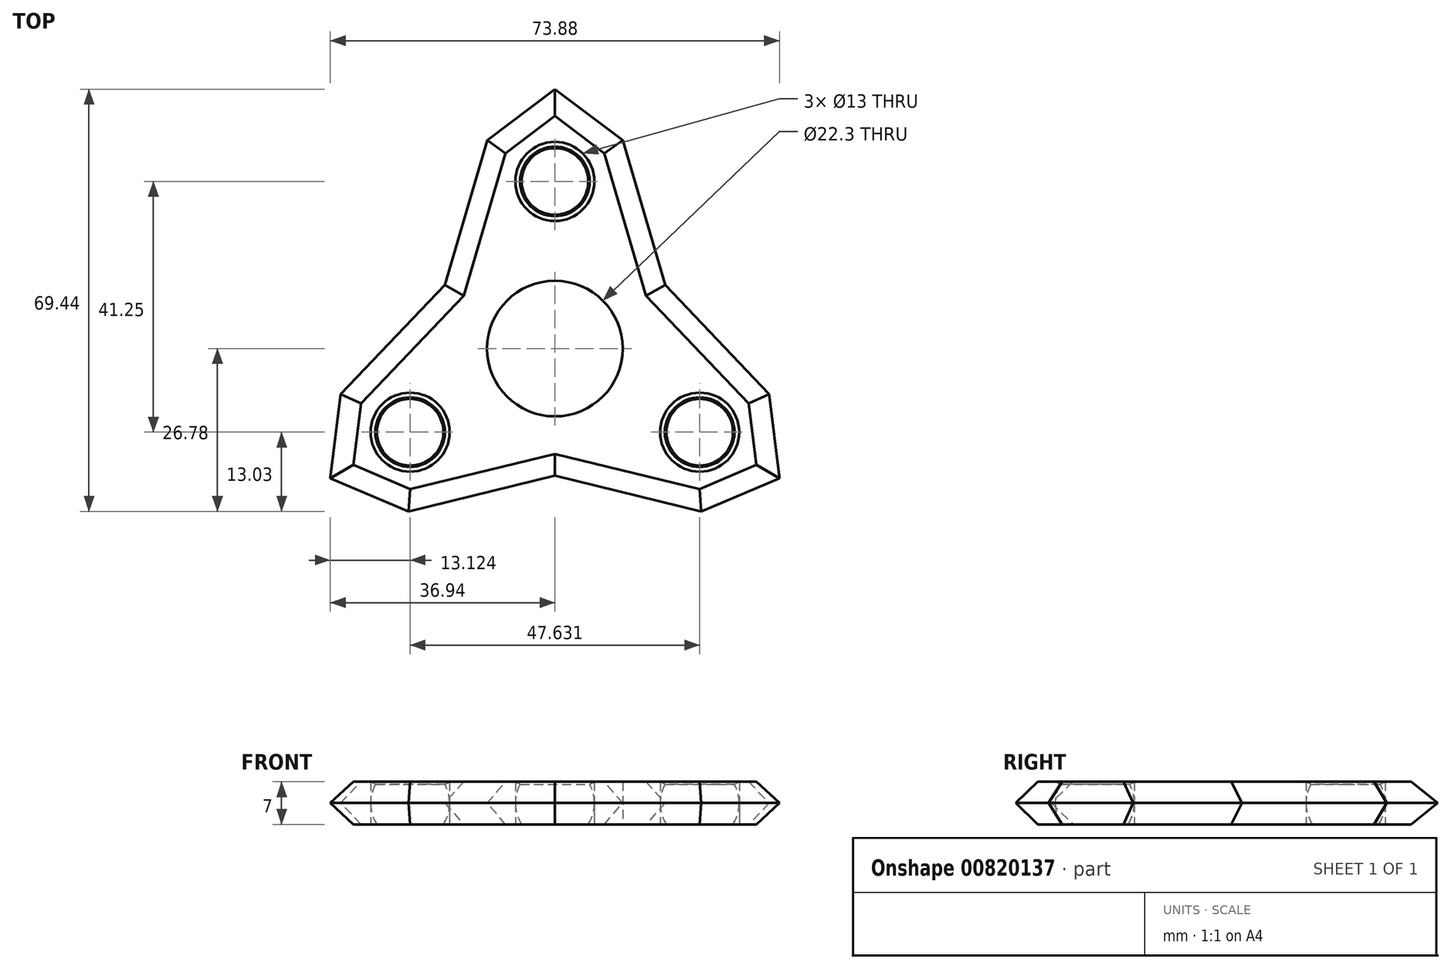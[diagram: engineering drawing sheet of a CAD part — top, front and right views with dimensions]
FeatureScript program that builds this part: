
annotation { "Feature Type Name" : "Feature", "Feature Type Description" : "" }
export const myFeature = defineFeature(function(context is Context, id is Id, definition is map)
    precondition{}
    {
        {
            var Q0;
            Q0=qCreatedBy(makeId("Top.planeOp"),FACE);
            var sketch = newSketch(context, id + "F0", { "sketchPlane" : qUnion([Q0])});
            skCircle(sketch, "E0", {"center": v(0, 0) * mm, "radius": 11.15 * mm});
            skCircle(sketch, "E1", {"center": v(0, 27.5) * mm, "radius": 6.5 * mm});
            skLineSegment(sketch, "E2", {"start": v(0, 27.5) * mm, "end": v(0, 0) * mm});
            skCircle(sketch, "E3", {"center": v(0, 0) * mm, "radius": 14.15 * mm});
            skCircle(sketch, "E4", {"center": v(0, 27.5) * mm, "radius": 9.5 * mm});
            skLineSegment(sketch, "E5", {"start": v(0, 42.66) * mm, "end": v(11.14, 34.25) * mm});
            skLineSegment(sketch, "E6", {"start": v(0, 0) * mm, "end": v(12.25, 7.08) * mm});
            skLineSegment(sketch, "E7", {"start": v(12.25, 7.08) * mm, "end": v(39.54, 22.83) * mm});
            skLineSegment(sketch, "E8", {"start": v(11.14, 34.25) * mm, "end": v(18.13, 10.46) * mm});
            skLineSegment(sketch, "E9.MirrorCS", {"start": v(35.23, -7.47) * mm, "end": v(18.13, 10.46) * mm});
            skLineSegment(sketch, "E10.MirrorCS", {"start": v(36.94, -21.33) * mm, "end": v(35.23, -7.47) * mm});
            skLineSegment(sketch, "E11.MirrorCS", {"start": v(0, 42.66) * mm, "end": v(-11.14, 34.25) * mm});
            skLineSegment(sketch, "E12.MirrorCS", {"start": v(-11.14, 34.25) * mm, "end": v(-18.13, 10.46) * mm});
            skLineSegment(sketch, "E13.MirrorCS", {"start": v(-35.23, -7.47) * mm, "end": v(-18.13, 10.46) * mm});
            skLineSegment(sketch, "E14.MirrorCS", {"start": v(-36.94, -21.33) * mm, "end": v(-35.23, -7.47) * mm});
            skLineSegment(sketch, "E15.MirrorCS", {"start": v(-24.09, -26.78) * mm, "end": v(0, -20.93) * mm});
            skLineSegment(sketch, "E16.MirrorCS", {"start": v(-36.94, -21.33) * mm, "end": v(-24.09, -26.78) * mm});
            skLineSegment(sketch, "E17.MirrorCS", {"start": v(24.09, -26.78) * mm, "end": v(0, -20.93) * mm});
            skLineSegment(sketch, "E18.MirrorCS", {"start": v(36.94, -21.33) * mm, "end": v(24.09, -26.78) * mm});
            skCircle(sketch, "E19.1.0", {"center": v(-23.82, -13.75) * mm, "radius": 9.5 * mm});
            skCircle(sketch, "E19.1.1", {"center": v(-23.82, -13.75) * mm, "radius": 6.5 * mm});
            skCircle(sketch, "E19.2.0", {"center": v(23.82, -13.75) * mm, "radius": 9.5 * mm});
            skCircle(sketch, "E19.2.1", {"center": v(23.82, -13.75) * mm, "radius": 6.5 * mm});
            skSolve(sketch);
        }
        {
            var Q0;
            {var subQ0=sQuery(id+"F0.wireOp",EDGE,"E2");var subQ1=sQuery(id+"F0.wireOp",EDGE,"E0");var subQ2=makeQuery(id+"F0.imprint","INTERSECT",VERTEX,{"derivedFrom":[subQ1,subQ0]});Q0=makeQuery(id+"F0.imprint","IMPRINT",FACE,{"disambiguationData":[TD([[makeQuery(id+"F0.imprint","IMPRINT",EDGE,{"disambiguationData":[TD([[subQ2,-1.0]])],"derivedFrom":subQ1}),-1.0]])]});}
            var Q1;
            Q1=makeQuery(id+"F0.imprint","IMPRINT",FACE,{"disambiguationData":[TD([[makeQuery(id+"F0.imprint","IMPRINT",EDGE,{"derivedFrom":sQuery(id+"F0.wireOp",EDGE,"E4")}),-1.0]])]});
            var Q2;
            {var subQ0=sQuery(id+"F0.wireOp",EDGE,"E2");var subQ1=sQuery(id+"F0.wireOp",EDGE,"E0");var subQ2=makeQuery(id+"F0.imprint","INTERSECT",VERTEX,{"derivedFrom":[subQ1,subQ0]});Q2=makeQuery(id+"F0.imprint","IMPRINT",FACE,{"disambiguationData":[TD([[makeQuery(id+"F0.imprint","IMPRINT",EDGE,{"disambiguationData":[TD([[subQ2,1.0]])],"derivedFrom":subQ1}),-1.0]])]});}
            var Q3;
            Q3=makeQuery(id+"F0.imprint","IMPRINT",FACE,{"disambiguationData":[TD([[makeQuery(id+"F0.imprint","IMPRINT",EDGE,{"derivedFrom":sQuery(id+"F0.wireOp",EDGE,"E19.2.0")}),1.0]])]});
            var Q4;
            Q4=makeQuery(id+"F0.imprint","IMPRINT",FACE,{"disambiguationData":[TD([[makeQuery(id+"F0.imprint","IMPRINT",EDGE,{"derivedFrom":sQuery(id+"F0.wireOp",EDGE,"E1")}),-1.0]])]});
            var Q5;
            Q5=makeQuery(id+"F0.imprint","IMPRINT",FACE,{"disambiguationData":[TD([[makeQuery(id+"F0.imprint","IMPRINT",EDGE,{"derivedFrom":sQuery(id+"F0.wireOp",EDGE,"E19.1.0")}),1.0]])]});
            extrude(context, id + "F1", {"entities" : qUnion([Q0, Q1, Q2, Q3, Q4, Q5]), "depth" : 7 * mm, "offsetDistance" : 25 * mm});
        }
        {
            var Q0;
            Q0=makeQuery(id+"F1.opExtrude","CAP_EDGE",EDGE,{"disambiguationData":[OSD([sQuery(id+"F0.wireOp",EDGE,"E15.MirrorCS")])],"isStart":true});
            var Q1;
            Q1=makeQuery(id+"F1.opExtrude","CAP_EDGE",EDGE,{"disambiguationData":[OSD([sQuery(id+"F0.wireOp",EDGE,"E16.MirrorCS")])],"isStart":true});
            var Q2;
            Q2=makeQuery(id+"F1.opExtrude","CAP_EDGE",EDGE,{"disambiguationData":[OSD([sQuery(id+"F0.wireOp",EDGE,"E14.MirrorCS")])],"isStart":true});
            var Q3;
            Q3=makeQuery(id+"F1.opExtrude","CAP_EDGE",EDGE,{"disambiguationData":[OSD([sQuery(id+"F0.wireOp",EDGE,"E13.MirrorCS")])],"isStart":true});
            var Q4;
            Q4=makeQuery(id+"F1.opExtrude","CAP_EDGE",EDGE,{"disambiguationData":[OSD([sQuery(id+"F0.wireOp",EDGE,"E12.MirrorCS")])],"isStart":true});
            var Q5;
            Q5=makeQuery(id+"F1.opExtrude","CAP_EDGE",EDGE,{"disambiguationData":[OSD([sQuery(id+"F0.wireOp",EDGE,"E11.MirrorCS")])],"isStart":true});
            var Q6;
            Q6=makeQuery(id+"F1.opExtrude","CAP_EDGE",EDGE,{"disambiguationData":[OSD([sQuery(id+"F0.wireOp",EDGE,"E5")])],"isStart":true});
            var Q7;
            Q7=makeQuery(id+"F1.opExtrude","CAP_EDGE",EDGE,{"disambiguationData":[OSD([sQuery(id+"F0.wireOp",EDGE,"E8")])],"isStart":true});
            var Q8;
            Q8=makeQuery(id+"F1.opExtrude","CAP_EDGE",EDGE,{"disambiguationData":[OSD([sQuery(id+"F0.wireOp",EDGE,"E9.MirrorCS")])],"isStart":true});
            var Q9;
            Q9=makeQuery(id+"F1.opExtrude","CAP_EDGE",EDGE,{"disambiguationData":[OSD([sQuery(id+"F0.wireOp",EDGE,"E10.MirrorCS")])],"isStart":true});
            var Q10;
            Q10=makeQuery(id+"F1.opExtrude","CAP_EDGE",EDGE,{"disambiguationData":[OSD([sQuery(id+"F0.wireOp",EDGE,"E18.MirrorCS")])],"isStart":true});
            var Q11;
            Q11=makeQuery(id+"F1.opExtrude","CAP_EDGE",EDGE,{"disambiguationData":[OSD([sQuery(id+"F0.wireOp",EDGE,"E17.MirrorCS")])],"isStart":true});
            var Q12;
            Q12=makeQuery(id+"F1.opExtrude","CAP_EDGE",EDGE,{"disambiguationData":[OSD([sQuery(id+"F0.wireOp",EDGE,"E5")])],"isStart":false});
            var Q13;
            Q13=makeQuery(id+"F1.opExtrude","CAP_EDGE",EDGE,{"disambiguationData":[OSD([sQuery(id+"F0.wireOp",EDGE,"E11.MirrorCS")])],"isStart":false});
            var Q14;
            Q14=makeQuery(id+"F1.opExtrude","CAP_EDGE",EDGE,{"disambiguationData":[OSD([sQuery(id+"F0.wireOp",EDGE,"E8")])],"isStart":false});
            var Q15;
            Q15=makeQuery(id+"F1.opExtrude","CAP_EDGE",EDGE,{"disambiguationData":[OSD([sQuery(id+"F0.wireOp",EDGE,"E9.MirrorCS")])],"isStart":false});
            var Q16;
            Q16=makeQuery(id+"F1.opExtrude","CAP_EDGE",EDGE,{"disambiguationData":[OSD([sQuery(id+"F0.wireOp",EDGE,"E10.MirrorCS")])],"isStart":false});
            var Q17;
            Q17=makeQuery(id+"F1.opExtrude","CAP_EDGE",EDGE,{"disambiguationData":[OSD([sQuery(id+"F0.wireOp",EDGE,"E18.MirrorCS")])],"isStart":false});
            var Q18;
            Q18=makeQuery(id+"F1.opExtrude","CAP_EDGE",EDGE,{"disambiguationData":[OSD([sQuery(id+"F0.wireOp",EDGE,"E17.MirrorCS")])],"isStart":false});
            var Q19;
            Q19=makeQuery(id+"F1.opExtrude","CAP_EDGE",EDGE,{"disambiguationData":[OSD([sQuery(id+"F0.wireOp",EDGE,"E15.MirrorCS")])],"isStart":false});
            var Q20;
            Q20=makeQuery(id+"F1.opExtrude","CAP_EDGE",EDGE,{"disambiguationData":[OSD([sQuery(id+"F0.wireOp",EDGE,"E16.MirrorCS")])],"isStart":false});
            var Q21;
            Q21=makeQuery(id+"F1.opExtrude","CAP_EDGE",EDGE,{"disambiguationData":[OSD([sQuery(id+"F0.wireOp",EDGE,"E14.MirrorCS")])],"isStart":false});
            var Q22;
            Q22=makeQuery(id+"F1.opExtrude","CAP_EDGE",EDGE,{"disambiguationData":[OSD([sQuery(id+"F0.wireOp",EDGE,"E13.MirrorCS")])],"isStart":false});
            var Q23;
            Q23=makeQuery(id+"F1.opExtrude","CAP_EDGE",EDGE,{"disambiguationData":[OSD([sQuery(id+"F0.wireOp",EDGE,"E12.MirrorCS")])],"isStart":false});
            chamfer(context, id + "F2", {"entities" : qUnion([Q0, Q1, Q2, Q3, Q4, Q5, Q6, Q7, Q8, Q9, Q10, Q11, Q12, Q13, Q14, Q15, Q16, Q17, Q18, Q19, Q20, Q21, Q22, Q23]), "width" : 3.5 * mm, "tangentPropagation" : true});
        }
        {
            var Q0;
            Q0=qCreatedBy(makeId("Right.planeOp"),FACE);
            var sketch = newSketch(context, id + "F3", { "sketchPlane" : qUnion([Q0])});
            skLineSegment(sketch, "E20.0", {"start": v(21, 7) * mm, "end": v(34, 7) * mm});
            skLineSegment(sketch, "E21", {"start": v(21, 0) * mm, "end": v(21, 7) * mm});
            skLineSegment(sketch, "E22", {"start": v(34, 7) * mm, "end": v(34, 0) * mm});
            skLineSegment(sketch, "E23.0", {"start": v(32.15, 0) * mm, "end": v(8.66, 0) * mm});
            skLineSegment(sketch, "E24.0", {"start": v(21, 0) * mm, "end": v(34, 0) * mm});
            skLineSegment(sketch, "E25", {"start": v(34, 0) * mm, "end": v(21, 7) * mm});
            skLineSegment(sketch, "E26", {"start": v(34, 7) * mm, "end": v(21, 0) * mm});
            skCircle(sketch, "E27", {"center": v(27.5, 3.5) * mm, "radius": 6.5 * mm});
            skLineSegment(sketch, "E28", {"start": v(27.5, 0) * mm, "end": v(27.5, 7) * mm});
            skLineSegment(sketch, "E29", {"start": v(0, 0) * mm, "end": v(0, 24.68) * mm});
            skSolve(sketch);
        }
        {
            var Q0;
            {var subQ1=sQuery(id+"F3.wireOp",EDGE,"E21");var subQ3=sQuery(id+"F3.wireOp",EDGE,"E27");var subQ4=makeQuery(id+"F3.imprint","INTERSECT",VERTEX,{"derivedFrom":[subQ1,subQ3]});Q0=makeQuery(id+"F3.imprint","IMPRINT",FACE,{"disambiguationData":[TD([[makeQuery(id+"F3.imprint","IMPRINT",EDGE,{"disambiguationData":[TD([[subQ4,1.0]])],"derivedFrom":subQ3}),-1.0]])]});}
            var Q1;
            {var subQ1=sQuery(id+"F3.wireOp",EDGE,"E21");var subQ3=sQuery(id+"F3.wireOp",EDGE,"E27");var subQ4=makeQuery(id+"F3.imprint","INTERSECT",VERTEX,{"derivedFrom":[subQ1,subQ3]});Q1=makeQuery(id+"F3.imprint","IMPRINT",FACE,{"disambiguationData":[TD([[makeQuery(id+"F3.imprint","IMPRINT",EDGE,{"disambiguationData":[TD([[subQ4,-1.0]])],"derivedFrom":subQ3}),-1.0]])]});}
            var Q2;
            {var subQ1=sQuery(id+"F3.wireOp",EDGE,"E23.0");var subQ3=sQuery(id+"F3.wireOp",EDGE,"E27");var subQ4=makeQuery(id+"F3.imprint","INTERSECT",VERTEX,{"derivedFrom":[subQ1,subQ3]});Q2=makeQuery(id+"F3.imprint","IMPRINT",FACE,{"disambiguationData":[TD([[makeQuery(id+"F3.imprint","IMPRINT",EDGE,{"disambiguationData":[TD([[subQ4,1.0]])],"derivedFrom":subQ3}),-1.0]])]});}
            var Q3;
            {var subQ1=sQuery(id+"F3.wireOp",EDGE,"E20.0");var subQ3=sQuery(id+"F3.wireOp",EDGE,"E27");var subQ4=makeQuery(id+"F3.imprint","INTERSECT",VERTEX,{"disambiguationData":[OD(1.0)],"derivedFrom":[subQ1,subQ3]});Q3=makeQuery(id+"F3.imprint","IMPRINT",FACE,{"disambiguationData":[TD([[makeQuery(id+"F3.imprint","IMPRINT",EDGE,{"disambiguationData":[TD([[subQ4,-1.0]])],"derivedFrom":subQ3}),-1.0]])]});}
            var Q4;
            Q4=sQuery(id+"F3.wireOp",EDGE,"E28");
            revolve(context, id + "F4", {"surfaceOperationType" : NewSurfaceOperationType.NEW, "entities" : qUnion([Q0, Q1, Q2, Q3]), "axis" : qUnion([Q4]), "revolveType" : RevolveType.FULL});
        }
        {
            var Q0;
            Q0=makeQuery(id+"F4.opRevolve","SWEPT_BODY",BODY,{"disambiguationData":[OSD([sQuery(id+"F3.wireOp",EDGE,"E21"),sQuery(id+"F3.wireOp",EDGE,"E23.0"),sQuery(id+"F3.wireOp",EDGE,"E27")])]});
            var Q1;
            Q1=makeQuery(id+"F4.opRevolve","SWEPT_BODY",BODY,{"disambiguationData":[OSD([sQuery(id+"F3.wireOp",EDGE,"E20.0"),sQuery(id+"F3.wireOp",EDGE,"E21"),sQuery(id+"F3.wireOp",EDGE,"E27")])]});
            var Q2;
            Q2=sQuery(id+"F3.wireOp",EDGE,"E29");
            circularPattern(context, id + "F5", {"entities" : qUnion([Q0, Q1]), "axis" : qUnion([Q2]), "angle" : 360 * degree, "instanceCount" : 3, "equalSpace" : true});
        }
    });
